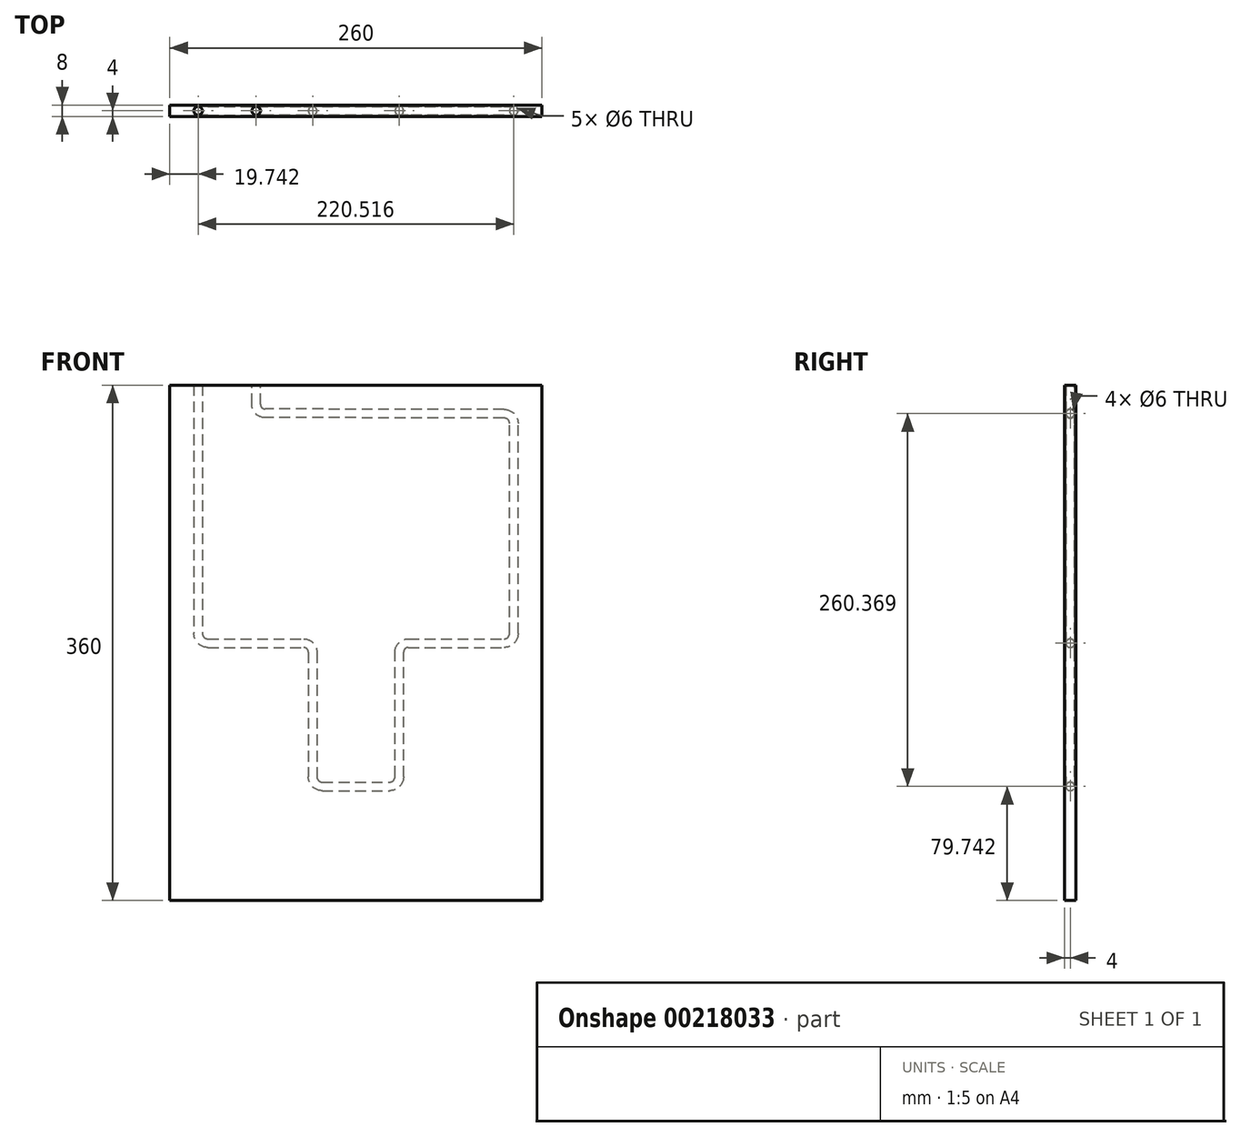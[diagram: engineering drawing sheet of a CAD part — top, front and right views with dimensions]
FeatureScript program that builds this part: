
annotation { "Feature Type Name" : "Feature", "Feature Type Description" : "" }
export const myFeature = defineFeature(function(context is Context, id is Id, definition is map)
    precondition{}
    {
        {
            var Q0;
            Q0=qCreatedBy(makeId("Front.planeOp"),FACE);
            var sketch = newSketch(context, id + "F0", { "sketchPlane" : qUnion([Q0])});
            skLineSegment(sketch, "E0.bottom", {"start": v(130, 180) * mm, "end": v(-130, 180) * mm});
            skLineSegment(sketch, "E0.top", {"start": v(130, -180) * mm, "end": v(-130, -180) * mm});
            skLineSegment(sketch, "E0.left", {"start": v(130, 180) * mm, "end": v(130, -180) * mm});
            skLineSegment(sketch, "E0.right", {"start": v(-130, 180) * mm, "end": v(-130, -180) * mm});
            skPoint(sketch, "E0.middle", {"position": v(0, 0) * mm});
            skSolve(sketch);
        }
        {
            var Q0;
            Q0=makeQuery(id+"F0.imprint","IMPRINT",FACE,{"disambiguationData":[TD([[makeQuery(id+"F0.imprint","IMPRINT",EDGE,{"derivedFrom":sQuery(id+"F0.wireOp",EDGE,"E0.bottom")}),1.0]])]});
            var sketch = newSketch(context, id + "F1", { "sketchPlane" : qUnion([Q0])});
            skLineSegment(sketch, "E1", {"start": v(-110, 200) * mm, "end": v(-110, 6.5) * mm});
            skLineSegment(sketch, "E2", {"start": v(-70, 200) * mm, "end": v(-70, 166.49) * mm});
            skLineSegment(sketch, "E3", {"start": v(-103.5, 0) * mm, "end": v(-36.5, 0) * mm});
            skLineSegment(sketch, "E4", {"start": v(-30, -6.5) * mm, "end": v(-30, -93.5) * mm});
            skLineSegment(sketch, "E5", {"start": v(-23.5, -100) * mm, "end": v(23.5, -100) * mm});
            skLineSegment(sketch, "E6", {"start": v(30, -93.5) * mm, "end": v(30, -6.5) * mm});
            skLineSegment(sketch, "E7", {"start": v(36.5, 0) * mm, "end": v(103.5, 0) * mm});
            skLineSegment(sketch, "E8", {"start": v(110, 6.5) * mm, "end": v(110, 153.21) * mm});
            skLineSegment(sketch, "E9", {"start": v(103.51, 159.71) * mm, "end": v(-63.51, 159.99) * mm});
            skPoint(sketch, "E10.visualSharp", {"position": v(-110, 0) * mm});
            skArc(sketch, "E10.filletArc", {"start": v(-110, 6.5) * mm, "mid": v(-108.1, 1.9) * mm, "end": v(-103.5, 0) * mm});
            skPoint(sketch, "E11.visualSharp", {"position": v(-30, 0) * mm});
            skArc(sketch, "E11.filletArc", {"start": v(-30, -6.5) * mm, "mid": v(-31.9, -1.9) * mm, "end": v(-36.5, 0) * mm});
            skPoint(sketch, "E12.visualSharp", {"position": v(-30, -100) * mm});
            skArc(sketch, "E12.filletArc", {"start": v(-30, -93.5) * mm, "mid": v(-28.1, -98.1) * mm, "end": v(-23.5, -100) * mm});
            skPoint(sketch, "E13.visualSharp", {"position": v(30, -100) * mm});
            skArc(sketch, "E13.filletArc", {"start": v(23.5, -100) * mm, "mid": v(28.1, -98.1) * mm, "end": v(30, -93.5) * mm});
            skPoint(sketch, "E14.visualSharp", {"position": v(30, 0) * mm});
            skArc(sketch, "E14.filletArc", {"start": v(36.5, 0) * mm, "mid": v(31.9, -1.9) * mm, "end": v(30, -6.5) * mm});
            skPoint(sketch, "E15.visualSharp", {"position": v(110, 0) * mm});
            skArc(sketch, "E15.filletArc", {"start": v(103.5, 0) * mm, "mid": v(108.1, 1.9) * mm, "end": v(110, 6.5) * mm});
            skPoint(sketch, "E16.visualSharp", {"position": v(110, 159.7) * mm});
            skArc(sketch, "E16.filletArc", {"start": v(110, 153.21) * mm, "mid": v(108.1, 157.8) * mm, "end": v(103.51, 159.71) * mm});
            skPoint(sketch, "E17.visualSharp", {"position": v(-70, 160) * mm});
            skArc(sketch, "E17.filletArc", {"start": v(-70, 166.49) * mm, "mid": v(-68.1, 161.9) * mm, "end": v(-63.51, 159.99) * mm});
            skSolve(sketch);
        }
        {
            var Q0;
            Q0=makeQuery(id+"F0.imprint","IMPRINT",FACE,{"disambiguationData":[TD([[makeQuery(id+"F0.imprint","IMPRINT",EDGE,{"derivedFrom":sQuery(id+"F0.wireOp",EDGE,"E0.bottom")}),1.0]])]});
            extrude(context, id + "F2", {"entities" : qUnion([Q0]), "depth" : 8 * mm, "symmetric" : true});
        }
        {
            var Q0;
            Q0=sQuery(id+"F1.wireOp",VERTEX,"E1.start");
            var Q1;
            Q1=qCreatedBy(makeId("Top.planeOp"),FACE);
            cPlane(context, id + "F3", {"entities" : qUnion([Q0, Q1]), "cplaneType" : CPlaneType.PLANE_POINT, "offset" : 25 * mm, "width" : 150 * mm, "height" : 150 * mm});
        }
        {
            var Q0;
            Q0=qCreatedBy(id+"F3.planeOp",FACE);
            var sketch = newSketch(context, id + "F4", { "sketchPlane" : qUnion([Q0])});
            skCircle(sketch, "E18", {"center": v(-110.26, 0) * mm, "radius": 3 * mm});
            skCircle(sketch, "E19", {"center": v(-70.07, 0) * mm, "radius": 3 * mm});
            skSolve(sketch);
        }
        {
            var Q0;
            Q0=makeQuery(id+"F4.imprint","IMPRINT",FACE,{"disambiguationData":[TD([[makeQuery(id+"F4.imprint","IMPRINT",EDGE,{"derivedFrom":sQuery(id+"F4.wireOp",EDGE,"E18")}),1.0]])]});
            var Q1;
            Q1=sQuery(id+"F1.wireOp",EDGE,"E1");
            var Q2;
            Q2=sQuery(id+"F1.wireOp",EDGE,"E10.filletArc");
            var Q3;
            Q3=sQuery(id+"F1.wireOp",EDGE,"E3");
            var Q4;
            Q4=sQuery(id+"F1.wireOp",EDGE,"E11.filletArc");
            var Q5;
            Q5=sQuery(id+"F1.wireOp",EDGE,"E4");
            var Q6;
            Q6=sQuery(id+"F1.wireOp",EDGE,"E12.filletArc");
            var Q7;
            Q7=sQuery(id+"F1.wireOp",EDGE,"E5");
            var Q8;
            Q8=sQuery(id+"F1.wireOp",EDGE,"E13.filletArc");
            var Q9;
            Q9=sQuery(id+"F1.wireOp",EDGE,"E6");
            var Q10;
            Q10=sQuery(id+"F1.wireOp",EDGE,"E14.filletArc");
            var Q11;
            Q11=sQuery(id+"F1.wireOp",EDGE,"E7");
            var Q12;
            Q12=sQuery(id+"F1.wireOp",EDGE,"E15.filletArc");
            var Q13;
            Q13=sQuery(id+"F1.wireOp",EDGE,"E8");
            var Q14;
            Q14=sQuery(id+"F1.wireOp",EDGE,"E16.filletArc");
            var Q15;
            Q15=sQuery(id+"F1.wireOp",EDGE,"E9");
            var Q16;
            Q16=sQuery(id+"F1.wireOp",EDGE,"E17.filletArc");
            var Q17;
            Q17=sQuery(id+"F1.wireOp",EDGE,"E2");
            sweep(context, id + "F5", {"operationType" : NewBodyOperationType.REMOVE, "profiles" : qUnion([Q0]), "path" : qUnion([Q1, Q2, Q3, Q4, Q5, Q6, Q7, Q8, Q9, Q10, Q11, Q12, Q13, Q14, Q15, Q16, Q17])});
        }
    });
